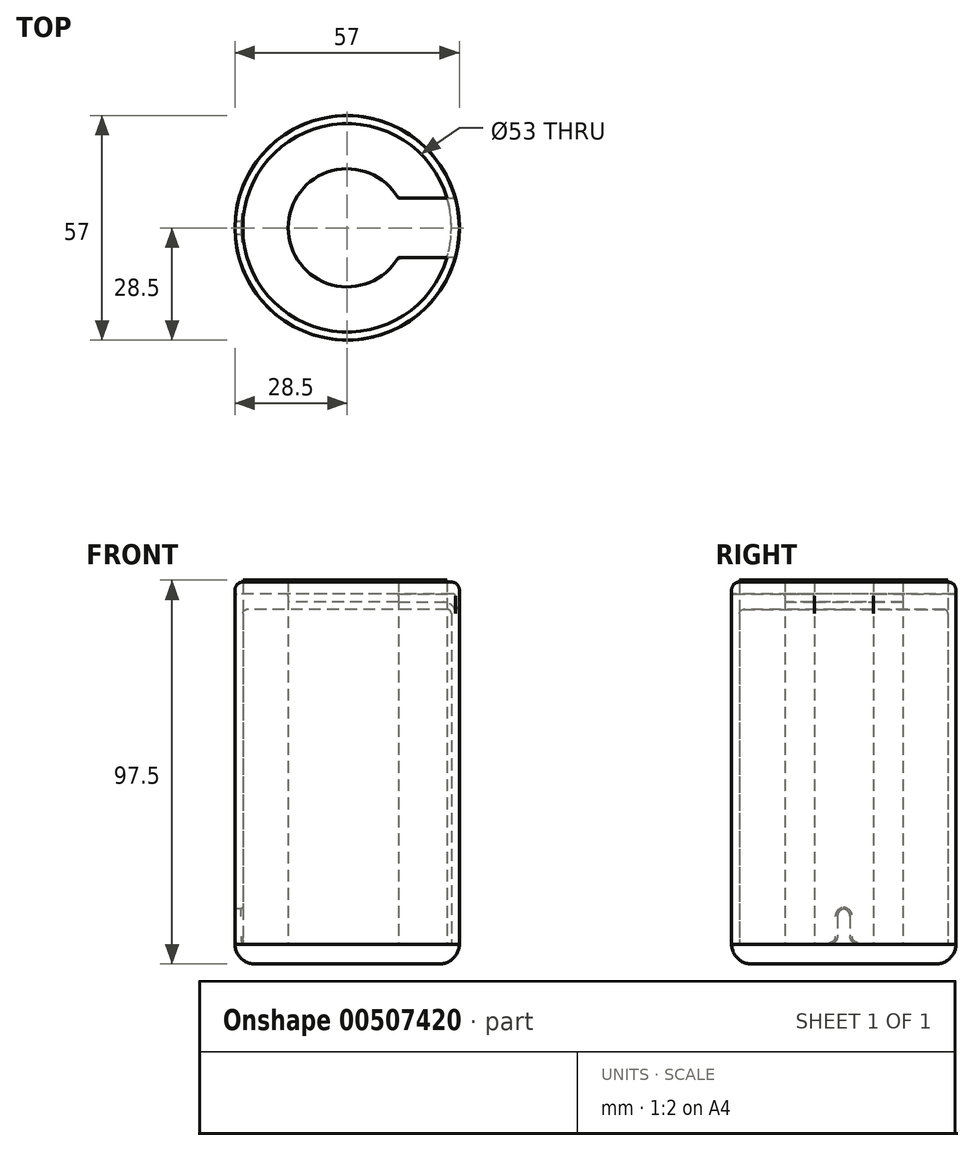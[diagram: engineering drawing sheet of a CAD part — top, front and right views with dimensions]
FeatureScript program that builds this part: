
annotation { "Feature Type Name" : "Feature", "Feature Type Description" : "" }
export const myFeature = defineFeature(function(context is Context, id is Id, definition is map)
    precondition{}
    {
        {
            var Q0;
            Q0=qCreatedBy(makeId("Top.planeOp"),FACE);
            var sketch = newSketch(context, id + "F0", { "sketchPlane" : qUnion([Q0])});
            skCircle(sketch, "E0", {"center": v(0, 0) * mm, "radius": 28.5 * mm});
            skCircle(sketch, "E1", {"center": v(0, 0) * mm, "radius": 26.5 * mm});
            skCircle(sketch, "E2", {"center": v(0, 0) * mm, "radius": 15 * mm});
            skLineSegment(sketch, "E3.bottom", {"start": v(-29.5, 1.6) * mm, "end": v(-25.5, 1.6) * mm});
            skLineSegment(sketch, "E3.top", {"start": v(-29.5, 0) * mm, "end": v(-25.5, 0) * mm});
            skLineSegment(sketch, "E3.left", {"start": v(-29.5, 1.6) * mm, "end": v(-29.5, 0) * mm});
            skLineSegment(sketch, "E3.right", {"start": v(-25.5, 1.6) * mm, "end": v(-25.5, 0) * mm});
            skLineSegment(sketch, "E4", {"start": v(-43.86, 0) * mm, "end": v(43.86, 0) * mm, "construction": true});
            skLineSegment(sketch, "E5.top", {"start": v(-29.5, -1.6) * mm, "end": v(-25.5, -1.6) * mm});
            skLineSegment(sketch, "E5.left", {"start": v(-29.5, 0) * mm, "end": v(-29.5, -1.6) * mm});
            skLineSegment(sketch, "E5.right", {"start": v(-25.5, 0) * mm, "end": v(-25.5, -1.6) * mm});
            skLineSegment(sketch, "E6.top", {"start": v(0, 7.5) * mm, "end": v(29.5, 7.5) * mm});
            skLineSegment(sketch, "E6.left", {"start": v(0, 0) * mm, "end": v(0, 7.5) * mm});
            skLineSegment(sketch, "E6.right", {"start": v(29.5, 0) * mm, "end": v(29.5, 7.5) * mm});
            skLineSegment(sketch, "E7.top", {"start": v(0, -7.5) * mm, "end": v(29.5, -7.5) * mm});
            skLineSegment(sketch, "E7.left", {"start": v(0, 0) * mm, "end": v(0, -7.5) * mm});
            skLineSegment(sketch, "E7.right", {"start": v(29.5, 0) * mm, "end": v(29.5, -7.5) * mm});
            skPoint(sketch, "E8", {"position": v(-28.5, 0) * mm});
            skPoint(sketch, "E9", {"position": v(-15, 0) * mm});
            skPoint(sketch, "E10", {"position": v(28.5, 0) * mm});
            skSolve(sketch);
        }
        {
            var Q0;
            {var subQ0=sQuery(id+"F0.wireOp",EDGE,"E6.top");var subQ1=sQuery(id+"F0.wireOp",EDGE,"E0");var subQ2=makeQuery(id+"F0.imprint","INTERSECT",VERTEX,{"derivedFrom":[subQ1,subQ0]});Q0=makeQuery(id+"F0.imprint","IMPRINT",FACE,{"disambiguationData":[TD([[makeQuery(id+"F0.imprint","IMPRINT",EDGE,{"disambiguationData":[TD([[subQ2,-1.0]])],"derivedFrom":subQ1}),1.0]])]});}
            var Q1;
            {var subQ9=sQuery(id+"F0.wireOp",EDGE,"E3.right");Q1=makeQuery(id+"F0.imprint","IMPRINT",FACE,{"disambiguationData":[TD([[makeQuery(id+"F0.imprint","IMPRINT",EDGE,{"derivedFrom":subQ9}),1.0]])]});}
            var Q2;
            {var subQ0=sQuery(id+"F0.wireOp",EDGE,"E5.top");var subQ1=sQuery(id+"F0.wireOp",EDGE,"E0");var subQ2=makeQuery(id+"F0.imprint","INTERSECT",VERTEX,{"derivedFrom":[subQ1,subQ0]});Q2=makeQuery(id+"F0.imprint","IMPRINT",FACE,{"disambiguationData":[TD([[makeQuery(id+"F0.imprint","IMPRINT",EDGE,{"disambiguationData":[TD([[subQ2,-1.0]])],"derivedFrom":subQ1}),1.0]])]});}
            var Q3;
            {var subQ0=sQuery(id+"F0.wireOp",EDGE,"E3.bottom");var subQ1=sQuery(id+"F0.wireOp",EDGE,"E0");var subQ2=makeQuery(id+"F0.imprint","INTERSECT",VERTEX,{"derivedFrom":[subQ1,subQ0]});Q3=makeQuery(id+"F0.imprint","IMPRINT",FACE,{"disambiguationData":[TD([[makeQuery(id+"F0.imprint","IMPRINT",EDGE,{"disambiguationData":[TD([[subQ2,-1.0]])],"derivedFrom":subQ1}),1.0]])]});}
            var Q4;
            {var subQ0=sQuery(id+"F0.wireOp",EDGE,"E5.top");var subQ1=sQuery(id+"F0.wireOp",EDGE,"E0");var subQ2=makeQuery(id+"F0.imprint","INTERSECT",VERTEX,{"derivedFrom":[subQ1,subQ0]});Q4=makeQuery(id+"F0.imprint","IMPRINT",FACE,{"disambiguationData":[TD([[makeQuery(id+"F0.imprint","IMPRINT",EDGE,{"disambiguationData":[TD([[subQ2,1.0]])],"derivedFrom":subQ1}),1.0]])]});}
            var Q5;
            {var subQ5=sQuery(id+"F0.wireOp",EDGE,"E3.right");Q5=makeQuery(id+"F0.imprint","IMPRINT",FACE,{"disambiguationData":[TD([[makeQuery(id+"F0.imprint","IMPRINT",EDGE,{"derivedFrom":subQ5}),-1.0]])]});}
            var Q6;
            {var subQ5=sQuery(id+"F0.wireOp",EDGE,"E5.right");Q6=makeQuery(id+"F0.imprint","IMPRINT",FACE,{"disambiguationData":[TD([[makeQuery(id+"F0.imprint","IMPRINT",EDGE,{"derivedFrom":subQ5}),-1.0]])]});}
            extrude(context, id + "F1", {"entities" : qUnion([Q0, Q1, Q2, Q3, Q4, Q5, Q6]), "depth" : 89 * mm, "offsetDistance" : 25 * mm});
        }
        {
            var Q0;
            {var subQ0=sQuery(id+"F0.wireOp",EDGE,"E6.left");Q0=makeQuery(id+"F0.imprint","IMPRINT",FACE,{"disambiguationData":[TD([[makeQuery(id+"F0.imprint","IMPRINT",EDGE,{"derivedFrom":subQ0}),1.0]])]});}
            var Q1;
            {var subQ5=sQuery(id+"F0.wireOp",EDGE,"E6.left");Q1=makeQuery(id+"F0.imprint","IMPRINT",FACE,{"disambiguationData":[TD([[makeQuery(id+"F0.imprint","IMPRINT",EDGE,{"derivedFrom":subQ5}),-1.0]])]});}
            var Q2;
            {var subQ5=sQuery(id+"F0.wireOp",EDGE,"E7.left");Q2=makeQuery(id+"F0.imprint","IMPRINT",FACE,{"disambiguationData":[TD([[makeQuery(id+"F0.imprint","IMPRINT",EDGE,{"derivedFrom":subQ5}),1.0]])]});}
            var Q3;
            {var subQ0=sQuery(id+"F0.wireOp",EDGE,"E7.bottom");var subQ1=sQuery(id+"F0.wireOp",EDGE,"E1");var subQ2=makeQuery(id+"F0.imprint","INTERSECT",VERTEX,{"derivedFrom":[subQ1,subQ0]});Q3=makeQuery(id+"F0.imprint","IMPRINT",FACE,{"disambiguationData":[TD([[makeQuery(id+"F0.imprint","IMPRINT",EDGE,{"disambiguationData":[TD([[subQ2,1.0]])],"derivedFrom":subQ1}),1.0]])]});}
            var Q4;
            {var subQ0=sQuery(id+"F0.wireOp",EDGE,"E6.top");var subQ1=sQuery(id+"F0.wireOp",EDGE,"E1");var subQ2=makeQuery(id+"F0.imprint","INTERSECT",VERTEX,{"derivedFrom":[subQ1,subQ0]});Q4=makeQuery(id+"F0.imprint","IMPRINT",FACE,{"disambiguationData":[TD([[makeQuery(id+"F0.imprint","IMPRINT",EDGE,{"disambiguationData":[TD([[subQ2,1.0]])],"derivedFrom":subQ1}),1.0]])]});}
            var Q5;
            {var subQ0=sQuery(id+"F0.wireOp",EDGE,"E6.top");var subQ1=sQuery(id+"F0.wireOp",EDGE,"E0");var subQ2=makeQuery(id+"F0.imprint","INTERSECT",VERTEX,{"derivedFrom":[subQ1,subQ0]});Q5=makeQuery(id+"F0.imprint","IMPRINT",FACE,{"disambiguationData":[TD([[makeQuery(id+"F0.imprint","IMPRINT",EDGE,{"disambiguationData":[TD([[subQ2,1.0]])],"derivedFrom":subQ1}),1.0]])]});}
            var Q6;
            {var subQ0=sQuery(id+"F0.wireOp",EDGE,"E7.top");var subQ1=sQuery(id+"F0.wireOp",EDGE,"E0");var subQ2=makeQuery(id+"F0.imprint","INTERSECT",VERTEX,{"derivedFrom":[subQ1,subQ0]});Q6=makeQuery(id+"F0.imprint","IMPRINT",FACE,{"disambiguationData":[TD([[makeQuery(id+"F0.imprint","IMPRINT",EDGE,{"disambiguationData":[TD([[subQ2,-1.0]])],"derivedFrom":subQ1}),1.0]])]});}
            extrude(context, id + "F2", {"entities" : qUnion([Q0, Q1, Q2, Q3, Q4, Q5, Q6]), "operationType" : NewBodyOperationType.ADD, "depth" : 87 * mm});
        }
        {
            var Q0;
            {var subQ9=sQuery(id+"F0.wireOp",EDGE,"E3.right");Q0=makeQuery(id+"F0.imprint","IMPRINT",FACE,{"disambiguationData":[TD([[makeQuery(id+"F0.imprint","IMPRINT",EDGE,{"derivedFrom":subQ9}),1.0]])]});}
            var Q1;
            {var subQ5=sQuery(id+"F0.wireOp",EDGE,"E3.right");Q1=makeQuery(id+"F0.imprint","IMPRINT",FACE,{"disambiguationData":[TD([[makeQuery(id+"F0.imprint","IMPRINT",EDGE,{"derivedFrom":subQ5}),-1.0]])]});}
            var Q2;
            {var subQ5=sQuery(id+"F0.wireOp",EDGE,"E5.right");Q2=makeQuery(id+"F0.imprint","IMPRINT",FACE,{"disambiguationData":[TD([[makeQuery(id+"F0.imprint","IMPRINT",EDGE,{"derivedFrom":subQ5}),-1.0]])]});}
            var Q3;
            {var subQ0=sQuery(id+"F0.wireOp",EDGE,"E6.left");Q3=makeQuery(id+"F0.imprint","IMPRINT",FACE,{"disambiguationData":[TD([[makeQuery(id+"F0.imprint","IMPRINT",EDGE,{"derivedFrom":subQ0}),1.0]])]});}
            var Q4;
            {var subQ5=sQuery(id+"F0.wireOp",EDGE,"E6.left");Q4=makeQuery(id+"F0.imprint","IMPRINT",FACE,{"disambiguationData":[TD([[makeQuery(id+"F0.imprint","IMPRINT",EDGE,{"derivedFrom":subQ5}),-1.0]])]});}
            var Q5;
            {var subQ5=sQuery(id+"F0.wireOp",EDGE,"E7.left");Q5=makeQuery(id+"F0.imprint","IMPRINT",FACE,{"disambiguationData":[TD([[makeQuery(id+"F0.imprint","IMPRINT",EDGE,{"derivedFrom":subQ5}),1.0]])]});}
            var Q6;
            {var subQ0=sQuery(id+"F0.wireOp",EDGE,"E7.bottom");var subQ1=sQuery(id+"F0.wireOp",EDGE,"E1");var subQ2=makeQuery(id+"F0.imprint","INTERSECT",VERTEX,{"derivedFrom":[subQ1,subQ0]});Q6=makeQuery(id+"F0.imprint","IMPRINT",FACE,{"disambiguationData":[TD([[makeQuery(id+"F0.imprint","IMPRINT",EDGE,{"disambiguationData":[TD([[subQ2,1.0]])],"derivedFrom":subQ1}),1.0]])]});}
            var Q7;
            {var subQ0=sQuery(id+"F0.wireOp",EDGE,"E6.top");var subQ1=sQuery(id+"F0.wireOp",EDGE,"E1");var subQ2=makeQuery(id+"F0.imprint","INTERSECT",VERTEX,{"derivedFrom":[subQ1,subQ0]});Q7=makeQuery(id+"F0.imprint","IMPRINT",FACE,{"disambiguationData":[TD([[makeQuery(id+"F0.imprint","IMPRINT",EDGE,{"disambiguationData":[TD([[subQ2,1.0]])],"derivedFrom":subQ1}),1.0]])]});}
            extrude(context, id + "F3", {"entities" : qUnion([Q0, Q1, Q2, Q3, Q4, Q5, Q6, Q7]), "operationType" : NewBodyOperationType.REMOVE, "oppositeDirection" : true, "depth" : -85 * mm, "hasSecondDirection" : true, "secondDirectionOppositeDirection" : true, "secondDirectionDepth" : 1 * mm});
        }
        {
            var Q0;
            {var subQ0=sQuery(id+"F0.wireOp",EDGE,"E3.bottom");var subQ1=sQuery(id+"F0.wireOp",EDGE,"E0");var subQ2=makeQuery(id+"F0.imprint","INTERSECT",VERTEX,{"derivedFrom":[subQ1,subQ0]});Q0=makeQuery(id+"F0.imprint","IMPRINT",FACE,{"disambiguationData":[TD([[makeQuery(id+"F0.imprint","IMPRINT",EDGE,{"disambiguationData":[TD([[subQ2,-1.0]])],"derivedFrom":subQ1}),1.0]])]});}
            var Q1;
            {var subQ0=sQuery(id+"F0.wireOp",EDGE,"E5.top");var subQ1=sQuery(id+"F0.wireOp",EDGE,"E0");var subQ2=makeQuery(id+"F0.imprint","INTERSECT",VERTEX,{"derivedFrom":[subQ1,subQ0]});Q1=makeQuery(id+"F0.imprint","IMPRINT",FACE,{"disambiguationData":[TD([[makeQuery(id+"F0.imprint","IMPRINT",EDGE,{"disambiguationData":[TD([[subQ2,1.0]])],"derivedFrom":subQ1}),1.0]])]});}
            extrude(context, id + "F4", {"entities" : qUnion([Q0, Q1]), "operationType" : NewBodyOperationType.REMOVE, "oppositeDirection" : true, "depth" : -9 * mm, "hasSecondDirection" : true, "secondDirectionOppositeDirection" : false, "secondDirectionDepth" : -1 * mm});
        }
        {
            var Q0;
            Q0=makeQuery(id+"F1.opExtrude","CAP_EDGE",EDGE,{"disambiguationData":[OSD([sQuery(id+"F0.wireOp",EDGE,"E2")])],"isStart":false});
            var Q1;
            Q1=makeQuery(id+"F1.opExtrude","CAP_EDGE",EDGE,{"disambiguationData":[OSD([sQuery(id+"F0.wireOp",EDGE,"E6.top")])],"isStart":false});
            var Q2;
            Q2=makeQuery(id+"F1.opExtrude","CAP_EDGE",EDGE,{"disambiguationData":[OSD([sQuery(id+"F0.wireOp",EDGE,"E0")])],"isStart":false});
            var Q3;
            Q3=makeQuery(id+"F1.opExtrude","CAP_EDGE",EDGE,{"disambiguationData":[OSD([sQuery(id+"F0.wireOp",EDGE,"E7.top")])],"isStart":false});
            fillet(context, id + "F5", {"entities" : qUnion([Q0, Q1, Q2, Q3]), "radius" : 0.5 * mm, "tangentPropagation" : true, "allowEdgeOverflow" : false});
        }
        {
            var Q0;
            Q0=makeQuery(id+"F2.opExtrude","CAP_EDGE",EDGE,{"disambiguationData":[OSD([sQuery(id+"F0.wireOp",EDGE,"E0")])],"isStart":false});
            fillet(context, id + "F6", {"entities" : qUnion([Q0]), "radius" : 3 * mm, "tangentPropagation" : true, "allowEdgeOverflow" : false});
        }
        {
            var Q0;
            Q0=makeQuery(id+"F3.boolean.opBoolean","COPY",EDGE,{"derivedFrom":makeQuery(id+"F3.opExtrude","CAP_EDGE",EDGE,{"disambiguationData":[OSD([sQuery(id+"F0.wireOp",EDGE,"E1")])],"isStart":false})});
            fillet(context, id + "F7", {"entities" : qUnion([Q0]), "radius" : 1 * mm, "tangentPropagation" : true, "allowEdgeOverflow" : false});
        }
        {
            var Q0;
            {var subQ0=sQuery(id+"F0.wireOp",EDGE,"E7.top");var subQ1=sQuery(id+"F0.wireOp",EDGE,"E6.top");var subQ2=sQuery(id+"F0.wireOp",EDGE,"E2");var subQ3=sQuery(id+"F0.wireOp",EDGE,"E0");Q0=makeQuery(id+"F4.boolean.opBoolean","INTERSECT",EDGE,{"derivedFrom":[makeQuery(id+"F2.boolean.opBoolean","MERGE",FACE,{"derivedFrom":[makeQuery(id+"F1.opExtrude","CAP_FACE",FACE,{"disambiguationData":[OSD([subQ3,subQ2,subQ1,subQ0])],"isStart":true}),makeQuery(id+"F2.opExtrude","CAP_FACE",FACE,{"disambiguationData":[OSD([subQ3,subQ2,subQ1,subQ0])],"isStart":true})]}),makeQuery(id+"F4.opExtrude","SWEPT_FACE",FACE,{"disambiguationData":[OSD([sQuery(id+"F0.wireOp",EDGE,"E3.bottom")])]})]});}
            var Q1;
            Q1=makeQuery(id+"F4.boolean.opBoolean","COPY",EDGE,{"derivedFrom":makeQuery(id+"F4.opExtrude","CAP_EDGE",EDGE,{"disambiguationData":[OSD([sQuery(id+"F0.wireOp",EDGE,"E3.bottom")])],"isStart":false})});
            var Q2;
            Q2=makeQuery(id+"F4.boolean.opBoolean","COPY",EDGE,{"derivedFrom":makeQuery(id+"F4.opExtrude","CAP_EDGE",EDGE,{"disambiguationData":[OSD([sQuery(id+"F0.wireOp",EDGE,"E5.top")])],"isStart":false})});
            var Q3;
            {var subQ0=sQuery(id+"F0.wireOp",EDGE,"E7.top");var subQ1=sQuery(id+"F0.wireOp",EDGE,"E6.top");var subQ2=sQuery(id+"F0.wireOp",EDGE,"E2");var subQ3=sQuery(id+"F0.wireOp",EDGE,"E0");Q3=makeQuery(id+"F4.boolean.opBoolean","INTERSECT",EDGE,{"derivedFrom":[makeQuery(id+"F2.boolean.opBoolean","MERGE",FACE,{"derivedFrom":[makeQuery(id+"F1.opExtrude","CAP_FACE",FACE,{"disambiguationData":[OSD([subQ3,subQ2,subQ1,subQ0])],"isStart":true}),makeQuery(id+"F2.opExtrude","CAP_FACE",FACE,{"disambiguationData":[OSD([subQ3,subQ2,subQ1,subQ0])],"isStart":true})]}),makeQuery(id+"F4.opExtrude","SWEPT_FACE",FACE,{"disambiguationData":[OSD([sQuery(id+"F0.wireOp",EDGE,"E5.top")])]})]});}
            fillet(context, id + "F8", {"entities" : qUnion([Q0, Q1, Q2, Q3]), "radius" : 2 * mm, "tangentPropagation" : true, "allowEdgeOverflow" : false});
        }
        {
            var Q0;
            {var subQ0=sQuery(id+"F0.wireOp",EDGE,"E7.top");var subQ1=sQuery(id+"F0.wireOp",EDGE,"E6.top");var subQ2=sQuery(id+"F0.wireOp",EDGE,"E2");var subQ3=sQuery(id+"F0.wireOp",EDGE,"E0");Q0=makeQuery(id+"F3.boolean.opBoolean","INTERSECT",EDGE,{"derivedFrom":[makeQuery(id+"F2.boolean.opBoolean","MERGE",FACE,{"derivedFrom":[makeQuery(id+"F1.opExtrude","CAP_FACE",FACE,{"disambiguationData":[OSD([subQ3,subQ2,subQ1,subQ0])],"isStart":true}),makeQuery(id+"F2.opExtrude","CAP_FACE",FACE,{"disambiguationData":[OSD([subQ3,subQ2,subQ1,subQ0])],"isStart":true})]}),makeQuery(id+"F3.opExtrude","SWEPT_FACE",FACE,{"disambiguationData":[OSD([sQuery(id+"F0.wireOp",EDGE,"E1")])]})]});}
            fillet(context, id + "F9", {"entities" : qUnion([Q0]), "radius" : 0.5 * mm, "tangentPropagation" : true, "allowEdgeOverflow" : false});
        }
        {
            var Q0;
            Q0=qCreatedBy(makeId("Top.planeOp"),FACE);
            var sketch = newSketch(context, id + "F10", { "sketchPlane" : qUnion([Q0])});
            skCircle(sketch, "E11", {"center": v(0, 0) * mm, "radius": 28.5 * mm});
            skCircle(sketch, "E12", {"center": v(0, 0) * mm, "radius": 26.5 * mm});
            skCircle(sketch, "E13", {"center": v(0, 0) * mm, "radius": 24.5 * mm});
            skSolve(sketch);
        }
        {
            var Q0;
            Q0=makeQuery(id+"F10.imprint","IMPRINT",FACE,{"disambiguationData":[TD([[makeQuery(id+"F10.imprint","IMPRINT",EDGE,{"derivedFrom":sQuery(id+"F10.wireOp",EDGE,"E12")}),1.0]])]});
            var Q1;
            Q1=makeQuery(id+"F10.imprint","IMPRINT",FACE,{"disambiguationData":[TD([[makeQuery(id+"F10.imprint","IMPRINT",EDGE,{"derivedFrom":sQuery(id+"F10.wireOp",EDGE,"E11")}),1.0]])]});
            var Q2;
            Q2=makeQuery(id+"F10.imprint","IMPRINT",FACE,{"disambiguationData":[TD([[makeQuery(id+"F10.imprint","IMPRINT",EDGE,{"derivedFrom":sQuery(id+"F10.wireOp",EDGE,"E13")}),1.0]])]});
            extrude(context, id + "F11", {"entities" : qUnion([Q0, Q1, Q2]), "depth" : -5 * mm});
        }
        {
            var Q0;
            Q0=makeQuery(id+"F11.opExtrude","CAP_EDGE",EDGE,{"disambiguationData":[OSD([sQuery(id+"F10.wireOp",EDGE,"E11")])],"isStart":false});
            fillet(context, id + "F12", {"entities" : qUnion([Q0]), "radius" : 5 * mm, "tangentPropagation" : true, "allowEdgeOverflow" : false});
        }
        {
            var Q0;
            {var subQ0=sQuery(id+"F0.wireOp",EDGE,"E3.bottom");var subQ1=sQuery(id+"F0.wireOp",EDGE,"E0");var subQ2=makeQuery(id+"F0.imprint","INTERSECT",VERTEX,{"derivedFrom":[subQ1,subQ0]});Q0=makeQuery(id+"F0.imprint","IMPRINT",FACE,{"disambiguationData":[TD([[makeQuery(id+"F0.imprint","IMPRINT",EDGE,{"disambiguationData":[TD([[subQ2,1.0]])],"derivedFrom":subQ1}),1.0]])]});}
            var Q1;
            {var subQ0=sQuery(id+"F0.wireOp",EDGE,"E5.top");var subQ1=sQuery(id+"F0.wireOp",EDGE,"E0");var subQ2=makeQuery(id+"F0.imprint","INTERSECT",VERTEX,{"derivedFrom":[subQ1,subQ0]});Q1=makeQuery(id+"F0.imprint","IMPRINT",FACE,{"disambiguationData":[TD([[makeQuery(id+"F0.imprint","IMPRINT",EDGE,{"disambiguationData":[TD([[subQ2,-1.0]])],"derivedFrom":subQ1}),1.0]])]});}
            var Q2;
            {var subQ0=sQuery(id+"F0.wireOp",EDGE,"E3.right");Q2=makeQuery(id+"F0.imprint","IMPRINT",FACE,{"disambiguationData":[TD([[makeQuery(id+"F0.imprint","IMPRINT",EDGE,{"derivedFrom":subQ0}),1.0]])]});}
            var Q3;
            {var subQ0=sQuery(id+"F0.wireOp",EDGE,"E3.bottom");var subQ1=sQuery(id+"F0.wireOp",EDGE,"E0");var subQ2=makeQuery(id+"F0.imprint","INTERSECT",VERTEX,{"derivedFrom":[subQ1,subQ0]});Q3=makeQuery(id+"F0.imprint","IMPRINT",FACE,{"disambiguationData":[TD([[makeQuery(id+"F0.imprint","IMPRINT",EDGE,{"disambiguationData":[TD([[subQ2,-1.0]])],"derivedFrom":subQ1}),1.0]])]});}
            var Q4;
            {var subQ0=sQuery(id+"F0.wireOp",EDGE,"E5.top");var subQ1=sQuery(id+"F0.wireOp",EDGE,"E0");var subQ2=makeQuery(id+"F0.imprint","INTERSECT",VERTEX,{"derivedFrom":[subQ1,subQ0]});Q4=makeQuery(id+"F0.imprint","IMPRINT",FACE,{"disambiguationData":[TD([[makeQuery(id+"F0.imprint","IMPRINT",EDGE,{"disambiguationData":[TD([[subQ2,1.0]])],"derivedFrom":subQ1}),1.0]])]});}
            var Q5;
            {var subQ5=sQuery(id+"F0.wireOp",EDGE,"E5.right");Q5=makeQuery(id+"F0.imprint","IMPRINT",FACE,{"disambiguationData":[TD([[makeQuery(id+"F0.imprint","IMPRINT",EDGE,{"derivedFrom":subQ5}),-1.0]])]});}
            var Q6;
            {var subQ5=sQuery(id+"F0.wireOp",EDGE,"E3.right");Q6=makeQuery(id+"F0.imprint","IMPRINT",FACE,{"disambiguationData":[TD([[makeQuery(id+"F0.imprint","IMPRINT",EDGE,{"derivedFrom":subQ5}),-1.0]])]});}
            var Q7;
            {var subQ4=sQuery(id+"F0.wireOp",EDGE,"E6.left");Q7=makeQuery(id+"F0.imprint","IMPRINT",FACE,{"disambiguationData":[TD([[makeQuery(id+"F0.imprint","IMPRINT",EDGE,{"derivedFrom":subQ4}),1.0]])]});}
            var Q8;
            {var subQ0=sQuery(id+"F0.wireOp",EDGE,"E6.left");Q8=makeQuery(id+"F0.imprint","IMPRINT",FACE,{"disambiguationData":[TD([[makeQuery(id+"F0.imprint","IMPRINT",EDGE,{"derivedFrom":subQ0}),-1.0]])]});}
            var Q9;
            {var subQ0=sQuery(id+"F0.wireOp",EDGE,"E6.top");var subQ1=sQuery(id+"F0.wireOp",EDGE,"E1");var subQ2=makeQuery(id+"F0.imprint","INTERSECT",VERTEX,{"derivedFrom":[subQ1,subQ0]});Q9=makeQuery(id+"F0.imprint","IMPRINT",FACE,{"disambiguationData":[TD([[makeQuery(id+"F0.imprint","IMPRINT",EDGE,{"disambiguationData":[TD([[subQ2,1.0]])],"derivedFrom":subQ1}),1.0]])]});}
            var Q10;
            {var subQ0=sQuery(id+"F0.wireOp",EDGE,"E6.top");var subQ1=sQuery(id+"F0.wireOp",EDGE,"E0");var subQ2=makeQuery(id+"F0.imprint","INTERSECT",VERTEX,{"derivedFrom":[subQ1,subQ0]});Q10=makeQuery(id+"F0.imprint","IMPRINT",FACE,{"disambiguationData":[TD([[makeQuery(id+"F0.imprint","IMPRINT",EDGE,{"disambiguationData":[TD([[subQ2,1.0]])],"derivedFrom":subQ1}),1.0]])]});}
            var Q11;
            Q11=sQuery(id+"F0.wireOp",EDGE,"E0");
            extrude(context, id + "F13", {"entities" : qUnion([Q0, Q1, Q2, Q3, Q4, Q5, Q6, Q7, Q8, Q9, Q10]), "surfaceEntities" : qUnion([Q11]), "depth" : 92 * mm, "offsetDistance" : 25 * mm});
        }
        {
            var Q0;
            Q0=makeQuery(id+"F13.opExtrude","CAP_EDGE",EDGE,{"disambiguationData":[OSD([sQuery(id+"F0.wireOp",EDGE,"E0")])],"isStart":false});
            fillet(context, id + "F14", {"entities" : qUnion([Q0]), "radius" : 2 * mm, "tangentPropagation" : true, "allowEdgeOverflow" : false});
        }
        {
            var Q0;
            {var subQ0=sQuery(id+"F0.wireOp",EDGE,"E3.right");Q0=makeQuery(id+"F0.imprint","IMPRINT",FACE,{"disambiguationData":[TD([[makeQuery(id+"F0.imprint","IMPRINT",EDGE,{"derivedFrom":subQ0}),1.0]])]});}
            var Q1;
            {var subQ5=sQuery(id+"F0.wireOp",EDGE,"E3.right");Q1=makeQuery(id+"F0.imprint","IMPRINT",FACE,{"disambiguationData":[TD([[makeQuery(id+"F0.imprint","IMPRINT",EDGE,{"derivedFrom":subQ5}),-1.0]])]});}
            var Q2;
            {var subQ5=sQuery(id+"F0.wireOp",EDGE,"E5.right");Q2=makeQuery(id+"F0.imprint","IMPRINT",FACE,{"disambiguationData":[TD([[makeQuery(id+"F0.imprint","IMPRINT",EDGE,{"derivedFrom":subQ5}),-1.0]])]});}
            extrude(context, id + "F15", {"entities" : qUnion([Q0, Q1, Q2]), "depth" : 92.5 * mm, "offsetDistance" : 25 * mm});
        }
    });
